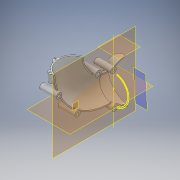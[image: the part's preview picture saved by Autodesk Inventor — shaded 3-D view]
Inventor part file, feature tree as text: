
AUTODESK INVENTOR PART (.ipt)
format: ipt  version: 2017 (Build 210142000, 142)  size: 461,312 bytes
history: native  units: mm
features: sketch x11, projected_geometry x6, other x4, extrude x4, sweep x1, loft x1, mirror x1
ambient origin geometry x8: Origin, YZ Plane, XZ Plane, XY Plane, X Axis, Y Axis, Z Axis, Center Point
bodies: Solide2 (feature_tree)
feature tree (28):
  sketch  "Esquisse1"
  sketch  "Esquisse2"
  other  "Plan de construction1"
  sketch  "Esquisse3"
  sketch  "Esquisse4"
  other  "Plan de construction2"
  sketch  "Esquisse6"
  sweep  "Balayage2"
  sketch  "Esquisse8"
  loft  "Lissage2"
  extrude  "Extrusion1"  Depth=54.0mm
  other  "Plan de construction3"
  extrude  "Extrusion3"  Depth=70.0mm
  extrude  "Extrusion4"  Depth=75.0mm
  mirror  "Symétrie1"
  extrude  "Extrusion5"  Depth=50.0mm
  sketch  "Esquisse7"
  projected_geometry  "Boucle projetée1"
  other  "Arêtes1"
  sketch  "Esquisse9"
  projected_geometry  "Boucle projetée2"
  projected_geometry  "Boucle projetée3"
  projected_geometry  "Boucle projetée4"
  projected_geometry  "Boucle projetée5"
  sketch  "Esquisse10"
  sketch  "Esquisse11"
  projected_geometry  "Boucle projetée6"
  sketch  "Esquisse12"
